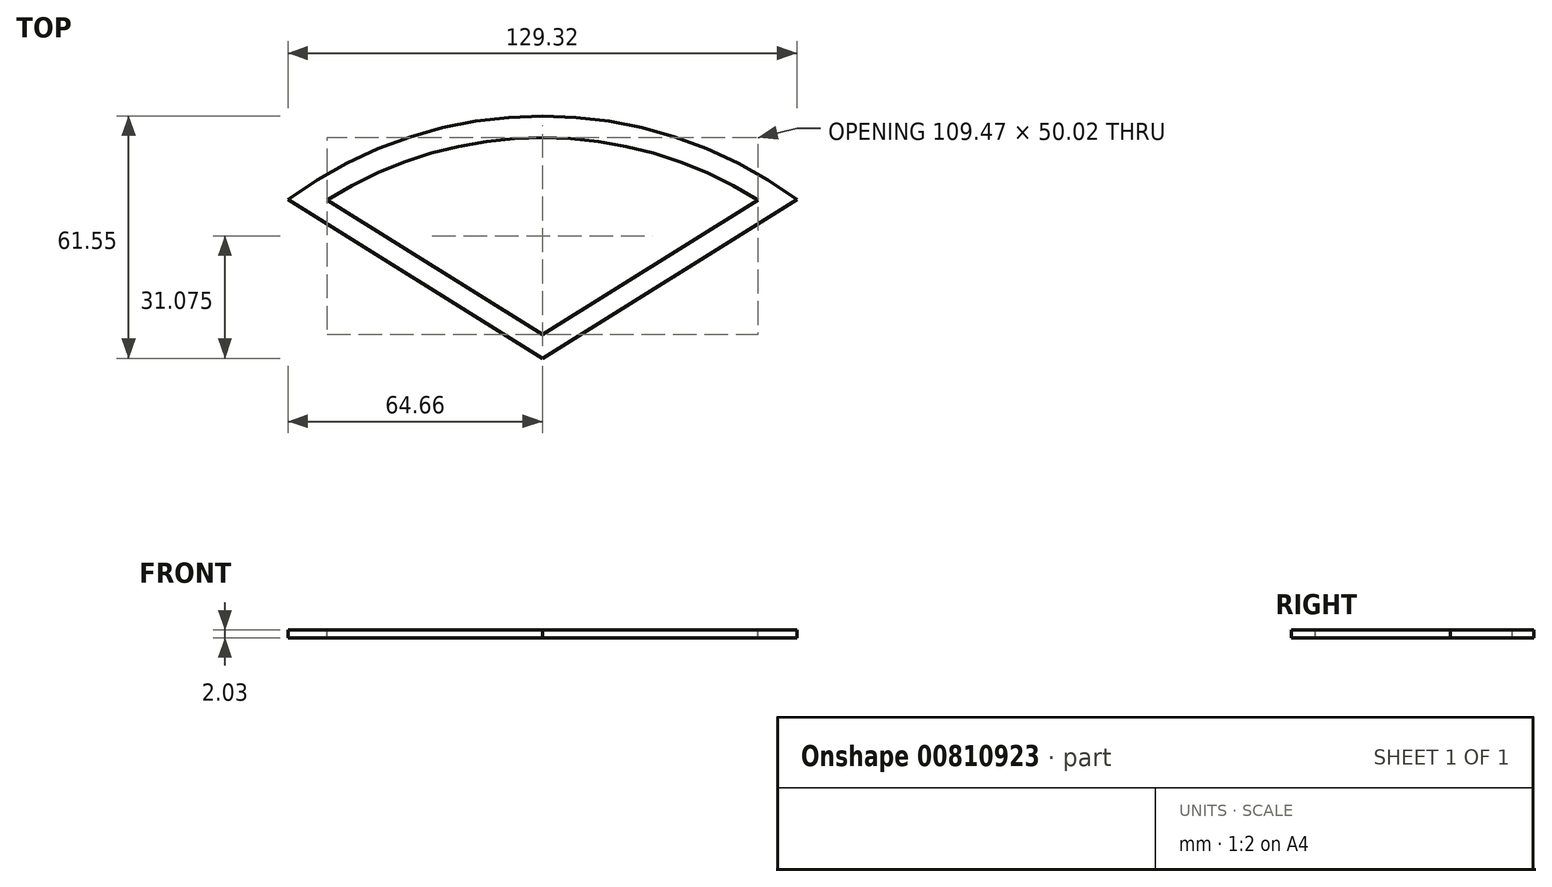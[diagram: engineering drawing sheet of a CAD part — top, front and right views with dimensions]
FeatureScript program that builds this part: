
annotation { "Feature Type Name" : "Feature", "Feature Type Description" : "" }
export const myFeature = defineFeature(function(context is Context, id is Id, definition is map)
    precondition{}
    {
        {
            var Q0;
            Q0=qCreatedBy(makeId("Top.planeOp"),FACE);
            var sketch = newSketch(context, id + "F0", { "sketchPlane" : qUnion([Q0])});
            skLineSegment(sketch, "E0", {"start": v(0, 0) * mm, "end": v(-64.66, 40.32) * mm});
            skLineSegment(sketch, "E1", {"start": v(0, 74.39) * mm, "end": v(0, -43.97) * mm});
            skLineSegment(sketch, "E2.MirrorCS", {"start": v(0, 0) * mm, "end": v(64.66, 40.32) * mm});
            skArc(sketch, "E3", {"start": v(64.66, 40.32) * mm, "mid": v(0, 61.55) * mm, "end": v(-64.66, 40.32) * mm});
            skSolve(sketch);
        }
        {
            var Q0;
            Q0 = qSketchRegion(id + "F0", true);
            extrude(context, id + "F1", {"entities" : qUnion([Q0]), "depth" : 2.03 * mm, "offsetDistance" : 25.4 * mm});
        }
        {
            var Q0;
            Q0=makeQuery(id+"F1.opExtrude","CAP_FACE",FACE,{"disambiguationData":[OSD([sQuery(id+"F0.wireOp",EDGE,"E0"),sQuery(id+"F0.wireOp",EDGE,"E2.MirrorCS"),sQuery(id+"F0.wireOp",EDGE,"E3")])],"isStart":false});
            var sketch = newSketch(context, id + "F2", { "sketchPlane" : qUnion([Q0])});
            skLineSegment(sketch, "E4", {"start": v(0, 6.07) * mm, "end": v(-54.74, 40.2) * mm});
            skLineSegment(sketch, "E5", {"start": v(0, 66.1) * mm, "end": v(0, -21.85) * mm});
            skLineSegment(sketch, "E6.MirrorCS", {"start": v(0, 6.07) * mm, "end": v(54.74, 40.2) * mm});
            skArc(sketch, "E7", {"start": v(54.74, 40.2) * mm, "mid": v(0, 56.08) * mm, "end": v(-54.74, 40.2) * mm});
            skSolve(sketch);
        }
        {
            var Q0;
            Q0 = qSketchRegion(id + "F2", true);
            extrude(context, id + "F3", {"entities" : qUnion([Q0]), "operationType" : NewBodyOperationType.REMOVE, "oppositeDirection" : true, "depth" : 25.4 * mm, "offsetDistance" : 25.4 * mm});
        }
    });
